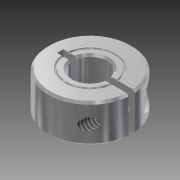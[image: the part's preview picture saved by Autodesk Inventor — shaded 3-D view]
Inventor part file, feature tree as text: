
AUTODESK INVENTOR PART (.ipt)
format: ipt  version: 2014 (Build 180170000, 170)  size: 384,000 bytes
history: native  units: mm
features: other x2, surface_op x1, thread x1
ambient origin geometry x8: Origin, YZ Plane, XZ Plane, XY Plane, X Axis, Y Axis, Z Axis, Center Point
bodies: Solid1 (feature_tree)
feature tree (4):
  surface_op  "Stitch Surface1"
  thread  "Thread1"  [1 undecoded]
  other  "Composite1"
  other  "Srf1"
note: 1 required parameter value undecoded (feature->parameter linkage not recoverable at this tier; creation-order binding heuristic only, values carry confidence <= 0.55)
